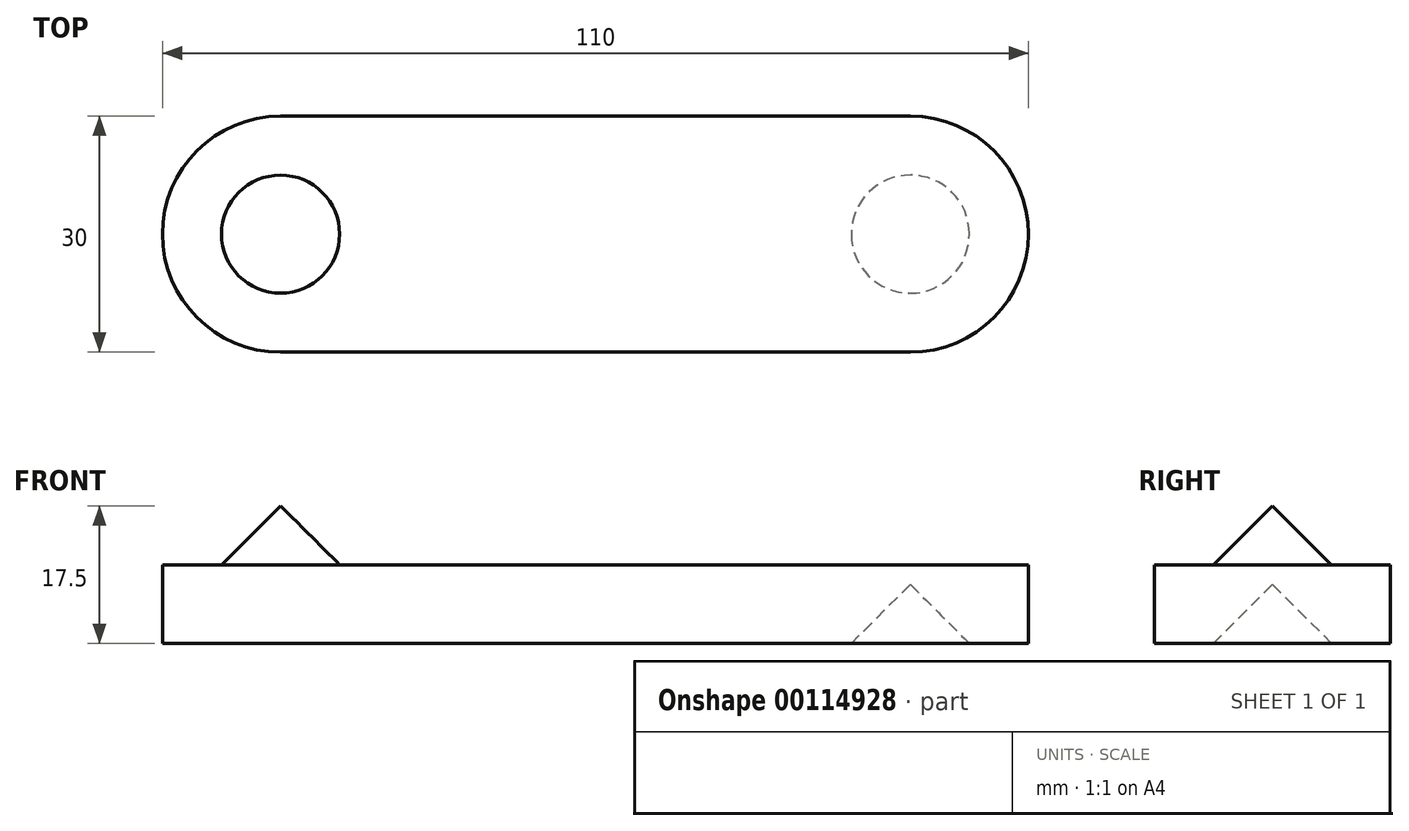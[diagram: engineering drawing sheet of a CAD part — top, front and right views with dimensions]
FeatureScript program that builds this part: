
annotation { "Feature Type Name" : "Feature", "Feature Type Description" : "" }
export const myFeature = defineFeature(function(context is Context, id is Id, definition is map)
    precondition{}
    {
        {
            var Q0;
            Q0=qCreatedBy(makeId("Top.planeOp"),FACE);
            var sketch = newSketch(context, id + "F0", { "sketchPlane" : qUnion([Q0])});
            skLineSegment(sketch, "E0.bottom", {"start": v(-28.28, 3.4) * mm, "end": v(51.72, 3.4) * mm});
            skLineSegment(sketch, "E0.top", {"start": v(-28.28, -26.6) * mm, "end": v(51.72, -26.6) * mm});
            skArc(sketch, "E1", {"start": v(-28.28, 3.4) * mm, "mid": v(-43.28, -11.6) * mm, "end": v(-28.28, -26.6) * mm});
            skArc(sketch, "E2", {"start": v(51.72, -26.6) * mm, "mid": v(66.72, -11.6) * mm, "end": v(51.72, 3.4) * mm});
            skSolve(sketch);
        }
        {
            var Q0;
            Q0 = qSketchRegion(id + "F0", true);
            extrude(context, id + "F1", {"entities" : qUnion([Q0]), "depth" : 10 * mm});
        }
        {
            var Q0;
            Q0=makeQuery(id+"F1.opExtrude","CAP_FACE",FACE,{"disambiguationData":[OSD([sQuery(id+"F0.wireOp",EDGE,"E0.bottom"),sQuery(id+"F0.wireOp",EDGE,"E0.top"),sQuery(id+"F0.wireOp",EDGE,"E1"),sQuery(id+"F0.wireOp",EDGE,"E2")])],"isStart":false});
            var sketch = newSketch(context, id + "F2", { "sketchPlane" : qUnion([Q0])});
            skCircle(sketch, "E3", {"center": v(-28.28, -11.6) * mm, "radius": 7.5 * mm});
            skSolve(sketch);
        }
        {
            var Q0;
            Q0=makeQuery(id+"F2.imprint","IMPRINT",FACE,{"disambiguationData":[TD([[makeQuery(id+"F2.imprint","IMPRINT",EDGE,{"derivedFrom":sQuery(id+"F2.wireOp",EDGE,"E3")}),1.0]])]});
            extrude(context, id + "F3", {"entities" : qUnion([Q0]), "operationType" : NewBodyOperationType.ADD, "depth" : 7.5 * mm, "hasDraft" : true, "draftAngle" : 45 * degree, "draftPullDirection" : true});
        }
        {
            var Q0;
            Q0=makeQuery(id+"F1.opExtrude","CAP_FACE",FACE,{"disambiguationData":[OSD([sQuery(id+"F0.wireOp",EDGE,"E0.bottom"),sQuery(id+"F0.wireOp",EDGE,"E0.top"),sQuery(id+"F0.wireOp",EDGE,"E1"),sQuery(id+"F0.wireOp",EDGE,"E2")])],"isStart":true});
            var sketch = newSketch(context, id + "F4", { "sketchPlane" : qUnion([Q0])});
            skCircle(sketch, "E4", {"center": v(51.72, 11.6) * mm, "radius": 7.5 * mm});
            skSolve(sketch);
        }
        {
            var Q0;
            Q0 = qSketchRegion(id + "F4", true);
            extrude(context, id + "F5", {"entities" : qUnion([Q0]), "operationType" : NewBodyOperationType.REMOVE, "oppositeDirection" : true, "depth" : 7.5 * mm, "hasDraft" : true, "draftAngle" : 45 * degree, "draftPullDirection" : true});
        }
    });
